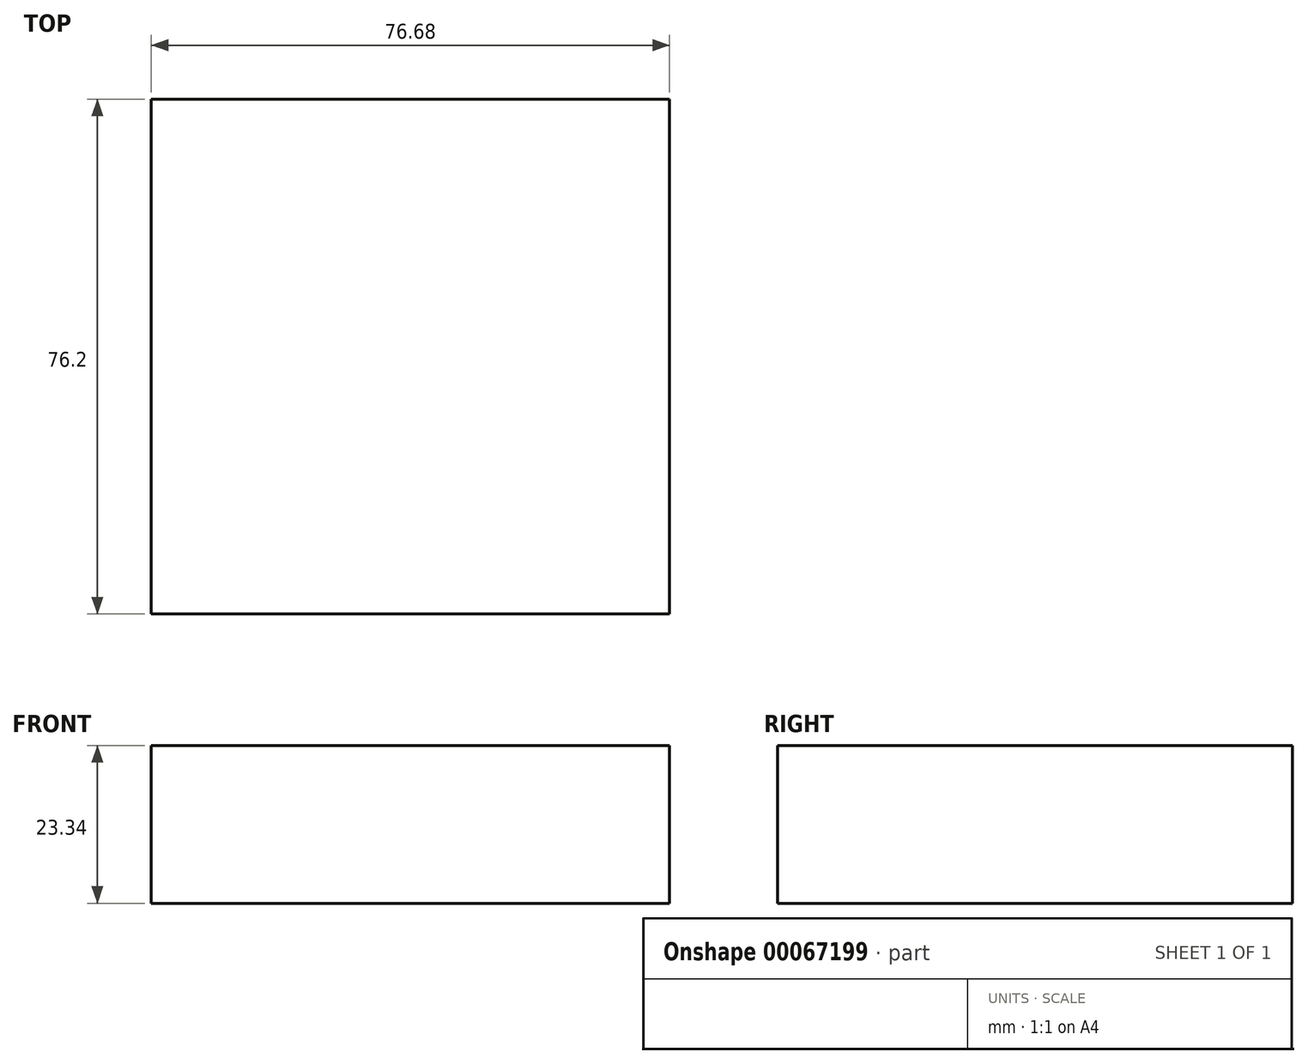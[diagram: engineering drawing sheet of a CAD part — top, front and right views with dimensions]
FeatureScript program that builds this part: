
annotation { "Feature Type Name" : "Feature", "Feature Type Description" : "" }
export const myFeature = defineFeature(function(context is Context, id is Id, definition is map)
    precondition{}
    {
        {
            var Q0;
            Q0=qCreatedBy(makeId("Front.planeOp"),FACE);
            var sketch = newSketch(context, id + "F0", { "sketchPlane" : qUnion([Q0])});
            skLineSegment(sketch, "E0.rect.bottom", {"start": v(38.34, -11.67) * mm, "end": v(-38.34, -11.67) * mm});
            skLineSegment(sketch, "E0.rect.top", {"start": v(38.34, 11.67) * mm, "end": v(-38.34, 11.67) * mm});
            skLineSegment(sketch, "E0.rect.left", {"start": v(38.34, -11.67) * mm, "end": v(38.34, 11.67) * mm});
            skLineSegment(sketch, "E0.rect.right", {"start": v(-38.34, -11.67) * mm, "end": v(-38.34, 11.67) * mm});
            skPoint(sketch, "E0.rect.middle", {"position": v(0, 0) * mm});
            skSolve(sketch);
        }
        {
            var Q0;
            Q0=makeQuery(id+"F0.imprint","IMPRINT",FACE,{"disambiguationData":[TD([[makeQuery(id+"F0.imprint","IMPRINT",EDGE,{"derivedFrom":sQuery(id+"F0.wireOp",EDGE,"E0.rect.bottom")}),-1.0]])]});
            extrude(context, id + "F1", {"entities" : qUnion([Q0]), "depth" : 76.2 * mm});
        }
    });
